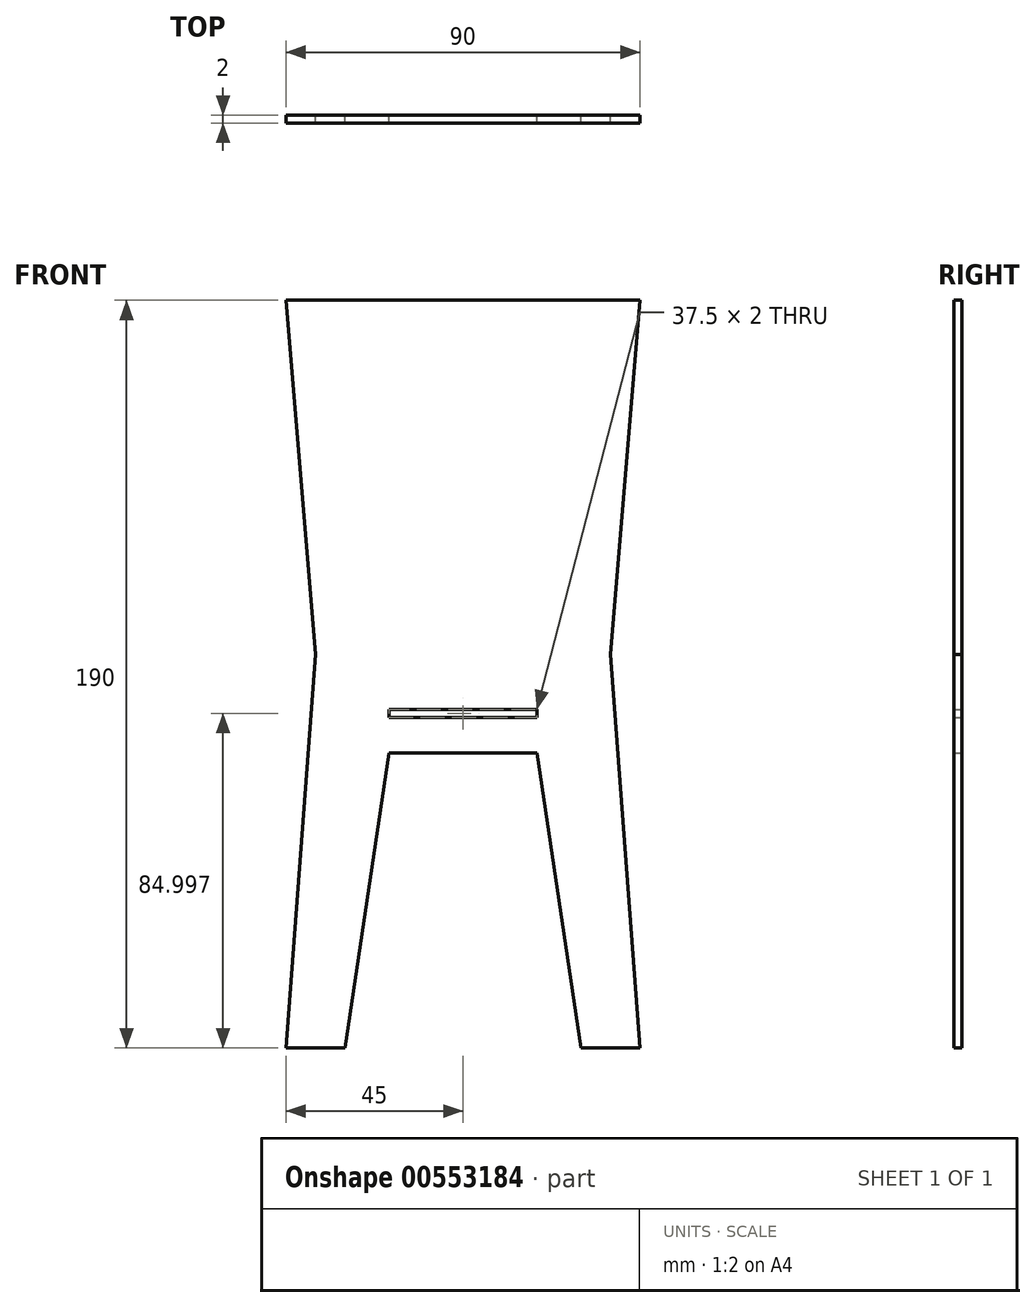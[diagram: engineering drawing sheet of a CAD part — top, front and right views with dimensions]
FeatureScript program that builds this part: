
annotation { "Feature Type Name" : "Feature", "Feature Type Description" : "" }
export const myFeature = defineFeature(function(context is Context, id is Id, definition is map)
    precondition{}
    {
        {
            var Q0;
            Q0=qCreatedBy(makeId("Front.planeOp"),FACE);
            var sketch = newSketch(context, id + "F0", { "sketchPlane" : qUnion([Q0])});
            skPoint(sketch, "E0.middle", {"position": v(0, -9.33) * mm});
            skLineSegment(sketch, "E1", {"start": v(-37.5, 40.67) * mm, "end": v(-45, -59.33) * mm});
            skLineSegment(sketch, "E2", {"start": v(37.5, 40.67) * mm, "end": v(45, -59.33) * mm});
            skLineSegment(sketch, "E3", {"start": v(-45, -59.33) * mm, "end": v(-30, -59.33) * mm});
            skLineSegment(sketch, "E4", {"start": v(45, -59.33) * mm, "end": v(30, -59.33) * mm});
            skPoint(sketch, "E5", {"position": v(18.75, 15.67) * mm});
            skPoint(sketch, "E6", {"position": v(-18.75, 15.67) * mm});
            skLineSegment(sketch, "E7", {"start": v(-18.75, 15.67) * mm, "end": v(-30, -59.33) * mm});
            skLineSegment(sketch, "E8", {"start": v(18.75, 15.67) * mm, "end": v(30, -59.33) * mm});
            skLineSegment(sketch, "E9", {"start": v(-18.75, 15.67) * mm, "end": v(18.75, 15.67) * mm});
            skLineSegment(sketch, "E10", {"start": v(-18.75, 24.67) * mm, "end": v(18.75, 24.67) * mm});
            skLineSegment(sketch, "E11", {"start": v(18.75, 24.67) * mm, "end": v(18.75, 26.67) * mm});
            skLineSegment(sketch, "E12", {"start": v(18.75, 26.67) * mm, "end": v(-18.75, 26.67) * mm});
            skLineSegment(sketch, "E13", {"start": v(-18.75, 26.67) * mm, "end": v(-18.75, 24.67) * mm});
            skLineSegment(sketch, "E14", {"start": v(45, 130.67) * mm, "end": v(37.5, 40.67) * mm});
            skLineSegment(sketch, "E15", {"start": v(-45, 130.67) * mm, "end": v(-37.5, 40.67) * mm});
            skLineSegment(sketch, "E16", {"start": v(-45, 130.67) * mm, "end": v(45, 130.67) * mm});
            skLineSegment(sketch, "E17", {"start": v(39.38, 15.67) * mm, "end": v(-39.38, 15.67) * mm});
            skSolve(sketch);
        }
        {
            var Q0;
            Q0 = qSketchRegion(id + "F0", true);
            extrude(context, id + "F1", {"entities" : qUnion([Q0]), "depth" : 2 * mm, "offsetDistance" : 25 * mm});
        }
    });
